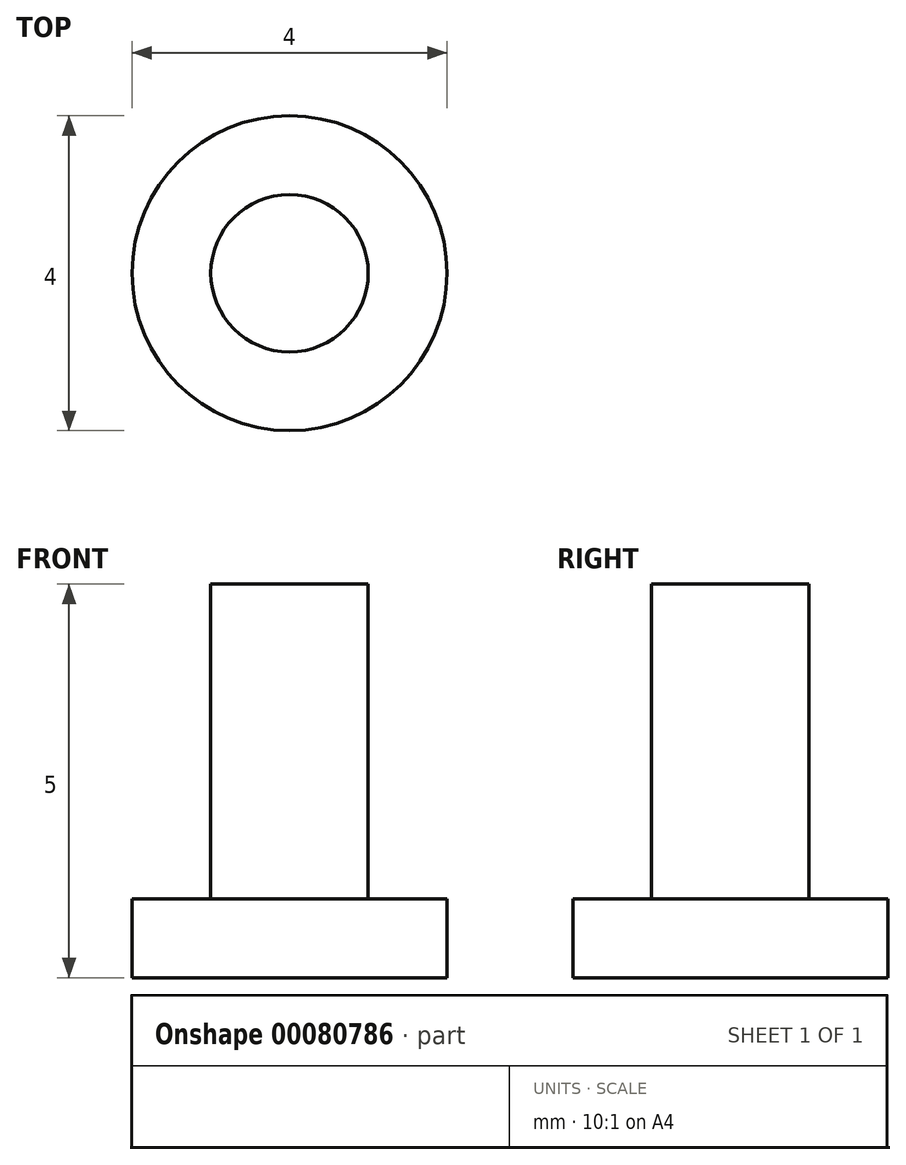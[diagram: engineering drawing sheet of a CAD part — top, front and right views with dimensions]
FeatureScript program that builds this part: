
annotation { "Feature Type Name" : "Feature", "Feature Type Description" : "" }
export const myFeature = defineFeature(function(context is Context, id is Id, definition is map)
    precondition{}
    {
        {
            var Q0;
            Q0=qCreatedBy(makeId("Top.planeOp"),FACE);
            var sketch = newSketch(context, id + "F0", { "sketchPlane" : qUnion([Q0])});
            skCircle(sketch, "E0", {"center": v(0, 0) * mm, "radius": 2 * mm});
            skSolve(sketch);
        }
        {
            var Q0;
            Q0=makeQuery(id+"F0.imprint","IMPRINT",FACE,{"disambiguationData":[TD([[makeQuery(id+"F0.imprint","IMPRINT",EDGE,{"derivedFrom":sQuery(id+"F0.wireOp",EDGE,"E0")}),1.0]])]});
            var sketch = newSketch(context, id + "F1", { "sketchPlane" : qUnion([Q0])});
            skCircle(sketch, "E1", {"center": v(0, 0) * mm, "radius": 1 * mm});
            skSolve(sketch);
        }
        {
            var Q0;
            Q0=makeQuery(id+"F0.imprint","IMPRINT",FACE,{"disambiguationData":[TD([[makeQuery(id+"F0.imprint","IMPRINT",EDGE,{"derivedFrom":sQuery(id+"F0.wireOp",EDGE,"E0")}),1.0]])]});
            extrude(context, id + "F2", {"entities" : qUnion([Q0]), "depth" : 1 * mm});
        }
        {
            var Q0;
            Q0=makeQuery(id+"F1.imprint","IMPRINT",FACE,{"disambiguationData":[TD([[makeQuery(id+"F1.imprint","IMPRINT",EDGE,{"derivedFrom":sQuery(id+"F1.wireOp",EDGE,"E1")}),1.0]])]});
            extrude(context, id + "F3", {"entities" : qUnion([Q0]), "operationType" : NewBodyOperationType.ADD, "depth" : 5 * mm});
        }
    });
